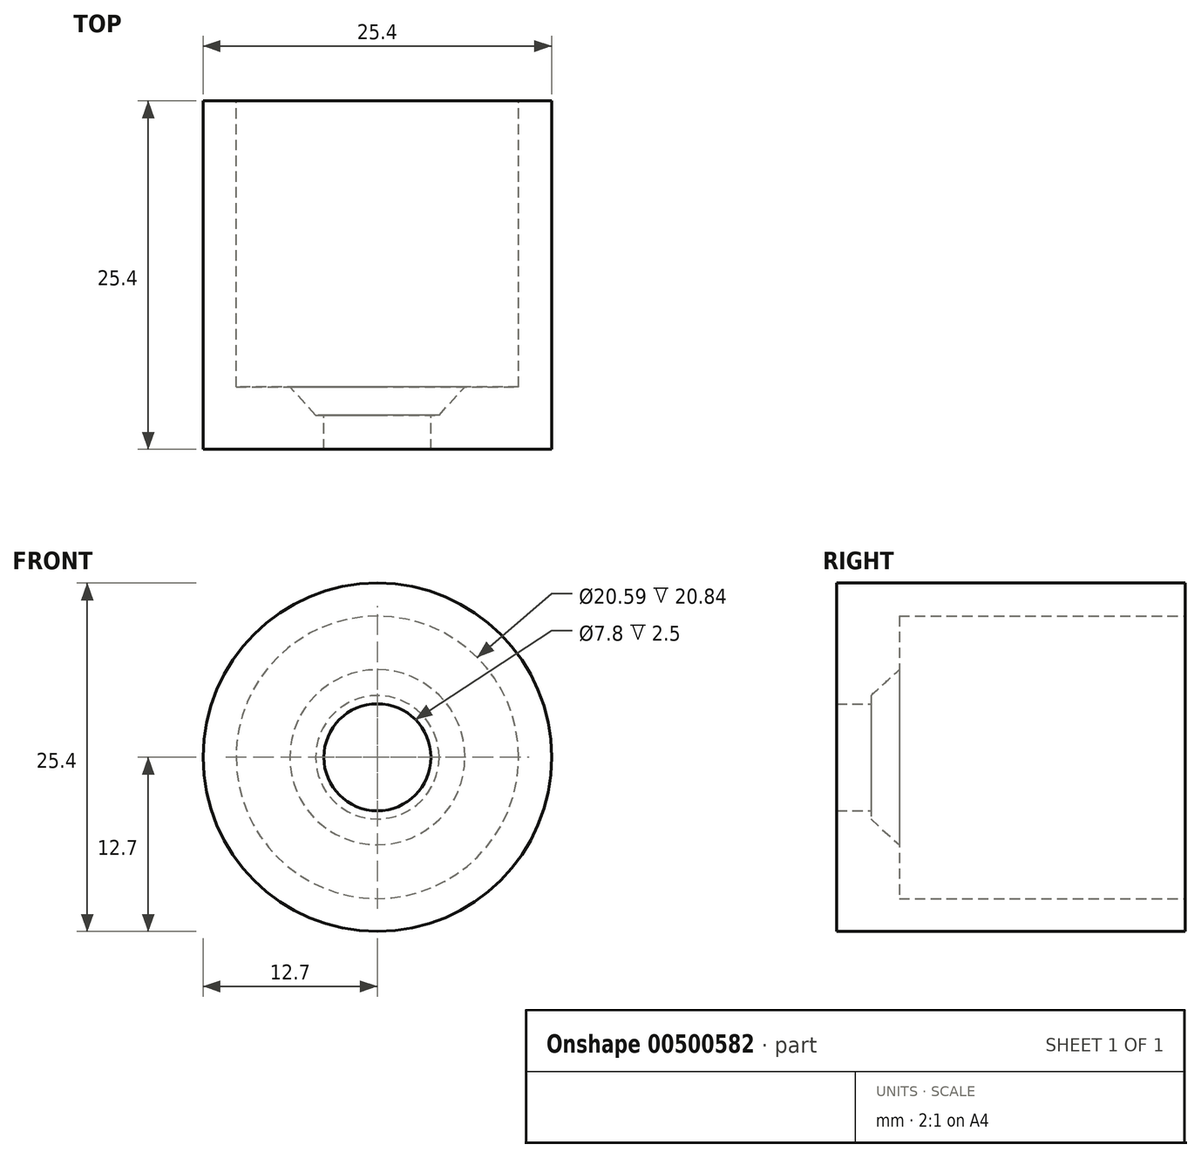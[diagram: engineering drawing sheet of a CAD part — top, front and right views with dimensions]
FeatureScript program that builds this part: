
annotation { "Feature Type Name" : "Feature", "Feature Type Description" : "" }
export const myFeature = defineFeature(function(context is Context, id is Id, definition is map)
    precondition{}
    {
        {
            var Q0;
            Q0=qCreatedBy(makeId("Top.planeOp"),FACE);
            var sketch = newSketch(context, id + "F0", { "sketchPlane" : qUnion([Q0])});
            skPoint(sketch, "E0", {"position": v(3.9, 0) * mm});
            skLineSegment(sketch, "E1", {"start": v(3.9, 0) * mm, "end": v(3.9, 2.5) * mm});
            skLineSegment(sketch, "E2", {"start": v(3.9, 2.5) * mm, "end": v(4.5, 2.5) * mm});
            skLineSegment(sketch, "E3", {"start": v(6.38, 4.56) * mm, "end": v(10.3, 4.56) * mm});
            skLineSegment(sketch, "E4", {"start": v(10.3, 4.56) * mm, "end": v(10.3, 25.4) * mm});
            skLineSegment(sketch, "E5", {"start": v(10.3, 25.4) * mm, "end": v(12.7, 25.4) * mm});
            skLineSegment(sketch, "E6", {"start": v(12.7, 25.4) * mm, "end": v(12.7, 0) * mm});
            skLineSegment(sketch, "E7", {"start": v(12.7, 0) * mm, "end": v(3.9, 0) * mm});
            skPoint(sketch, "E8", {"position": v(4.5, 2.5) * mm});
            skPoint(sketch, "E9", {"position": v(6.38, 4.56) * mm});
            skLineSegment(sketch, "E10", {"start": v(4.5, 2.5) * mm, "end": v(6.38, 4.56) * mm});
            skLineSegment(sketch, "E11", {"start": v(0, 0) * mm, "end": v(0, -4.42) * mm});
            skSolve(sketch);
        }
        {
            var Q0;
            Q0=makeQuery(id+"F0.imprint","IMPRINT",FACE,{"disambiguationData":[TD([[makeQuery(id+"F0.imprint","IMPRINT",EDGE,{"derivedFrom":sQuery(id+"F0.wireOp",EDGE,"E1")}),-1.0]])]});
            var Q1;
            Q1=sQuery(id+"F0.wireOp",EDGE,"E11");
            revolve(context, id + "F1", {"entities" : qUnion([Q0]), "axis" : qUnion([Q1]), "revolveType" : RevolveType.FULL});
        }
    });
